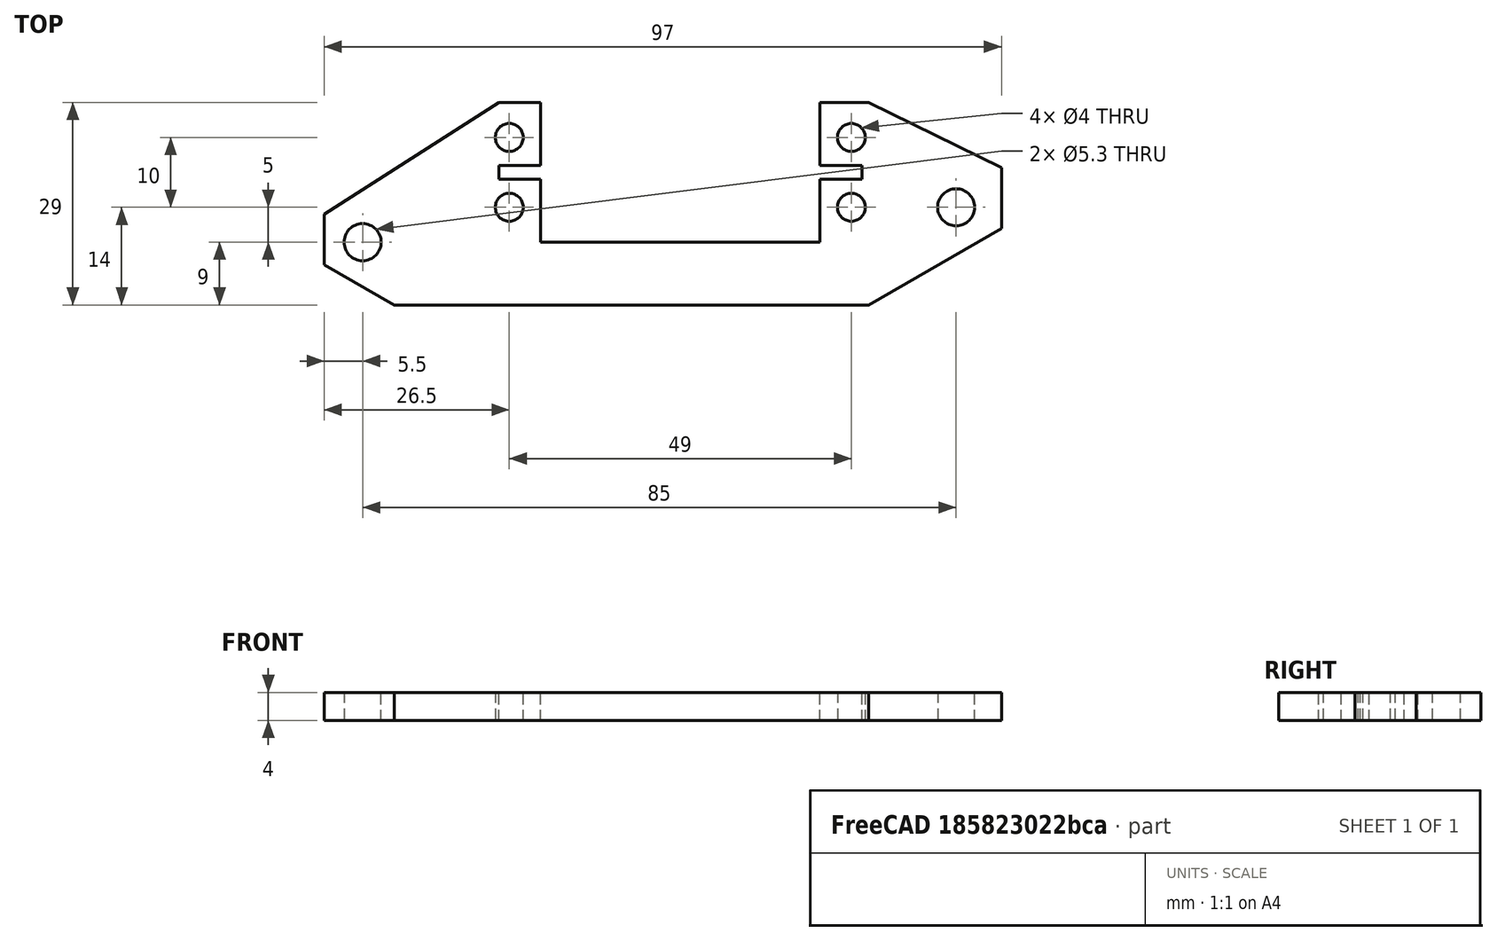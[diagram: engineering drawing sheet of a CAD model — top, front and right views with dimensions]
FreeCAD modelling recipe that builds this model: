
FCSTD DOCUMENT  (FreeCAD 0.19R24276 (Git))
Label: Servo_support_V4_long_oppozite_side_V1
License: All rights reserved
LicenseURL: http://en.wikipedia.org/wiki/All_rights_reserved
objects: Sketcher::SketchObject×1, PartDesign::Pad×1, PartDesign::Body×1
note: 4 computed .brp shape members not serialized (recipe doc carries the construction recipe); baked Part::Feature solids carry a one-line shape summary decoded from their .brp

FEATURE [Sketcher::SketchObject] Sketch005  label="Sketch005_54x20"
  AttachmentOffset = pos=(0,0,-5) rot=(0,0,1;0rad)
  FullyConstrained = false
  MapMode = 5
  Placement = pos=(0,0,-3) rot=(0,0,1;0rad)
  sketch-geometry (44):
    g0: GeomPoint X=1 Y=0 Z=0
    g1: GeomPoint X=1 Y=0 Z=0
    g2: GeomPoint X=1 Y=0 Z=0
    g3: GeomPoint X=1 Y=0 Z=0
    g4: Circle CenterX=-23.5 CenterY=5 CenterZ=0 NormalX=0 NormalY=0 NormalZ=1 AngleXU=0 Radius=2
    g5: Circle CenterX=-23.5 CenterY=-5 CenterZ=0 NormalX=0 NormalY=0 NormalZ=1 AngleXU=0 Radius=2
    g6: LineSegment StartX=1 StartY=0 StartZ=0 EndX=1 EndY=-5 EndZ=0
    g7: Circle CenterX=25.5 CenterY=5 CenterZ=0 NormalX=0 NormalY=0 NormalZ=1 AngleXU=0 Radius=2
    g8: Circle CenterX=25.5 CenterY=-5 CenterZ=0 NormalX=0 NormalY=0 NormalZ=1 AngleXU=0 Radius=2
    g9: LineSegment StartX=1 StartY=0 StartZ=0 EndX=-23.5 EndY=0 EndZ=0
    g10: LineSegment StartX=1 StartY=0 StartZ=0 EndX=49.8748 EndY=0 EndZ=0
    g11: ArcOfCircle CenterX=-7.75 CenterY=13.4234 CenterZ=0 NormalX=0 NormalY=0 NormalZ=1 AngleXU=0 Radius=9 StartAngle=0.290352 EndAngle=2.85124
    g12: LineSegment StartX=0 StartY=0 StartZ=0 EndX=-7.75 EndY=13.4234 EndZ=0
    g13: Circle CenterX=-44.5 CenterY=0 CenterZ=0 NormalX=0 NormalY=0 NormalZ=1 AngleXU=0 Radius=2.65
    g14: LineSegment StartX=-50 StartY=-19 StartZ=0 EndX=47 EndY=-19 EndZ=0
    g15: Circle CenterX=-44.5 CenterY=0 CenterZ=0 NormalX=0 NormalY=0 NormalZ=1 AngleXU=0 Radius=5.5
    g16: LineSegment StartX=-25 StartY=10 StartZ=0 EndX=-19 EndY=10 EndZ=0
    g17: LineSegment StartX=47 StartY=0.7 StartZ=0 EndX=47 EndY=-8.03034 EndZ=0
    g18: LineSegment StartX=-19 StartY=-10 StartZ=0 EndX=21 EndY=-10 EndZ=0
    g19: LineSegment StartX=21 StartY=-10 StartZ=0 EndX=21 EndY=-1 EndZ=0
    g20: Circle CenterX=40.5 CenterY=-5 CenterZ=0 NormalX=0 NormalY=0 NormalZ=1 AngleXU=0 Radius=2.65
    g21: Circle CenterX=40.5 CenterY=-5 CenterZ=0 NormalX=0 NormalY=0 NormalZ=1 AngleXU=0 Radius=5.5
    g22: LineSegment StartX=-19 StartY=-10 StartZ=0 EndX=-19 EndY=-1 EndZ=0
    g23: LineSegment StartX=-25 StartY=10 StartZ=0 EndX=-50 EndY=-6 EndZ=0
    g24: LineSegment StartX=-50 StartY=-6 StartZ=0 EndX=-50 EndY=-19 EndZ=0
    g25: LineSegment StartX=-50 StartY=-13.2265 StartZ=0 EndX=-40 EndY=-19 EndZ=0
    g26: LineSegment StartX=28 StartY=-19 StartZ=0 EndX=47 EndY=-8.03034 EndZ=0
    g27: LineSegment StartX=-50 StartY=-6 StartZ=0 EndX=-50 EndY=-13.2265 EndZ=0
    g28: LineSegment StartX=-40 StartY=-19 StartZ=0 EndX=28 EndY=-19 EndZ=0
    g29: LineSegment StartX=-25 StartY=1 StartZ=0 EndX=-19 EndY=1 EndZ=0
    g30: LineSegment StartX=-19 StartY=-1 StartZ=0 EndX=-25 EndY=-1 EndZ=0
    g31: LineSegment StartX=-25 StartY=-1 StartZ=0 EndX=-25 EndY=1 EndZ=0
    g32: LineSegment StartX=21 StartY=1 StartZ=0 EndX=27 EndY=1 EndZ=0
    g33: LineSegment StartX=27 StartY=1 StartZ=0 EndX=27 EndY=-1 EndZ=0
    g34: LineSegment StartX=27 StartY=-1 StartZ=0 EndX=21 EndY=-1 EndZ=0
    g35: LineSegment StartX=7.12713 StartY=-1 StartZ=0 EndX=7.12713 EndY=1 EndZ=0
    g36: LineSegment StartX=-23.5 StartY=0 StartZ=0 EndX=-25 EndY=0 EndZ=0
    g37: LineSegment StartX=-19 StartY=1 StartZ=0 EndX=-19 EndY=10 EndZ=0
    g38: LineSegment StartX=21 StartY=1 StartZ=0 EndX=21 EndY=10 EndZ=0
    g39: LineSegment StartX=21 StartY=10 StartZ=0 EndX=28 EndY=10 EndZ=0
    g40: LineSegment StartX=47 StartY=0.7 StartZ=0 EndX=28 EndY=10 EndZ=0
    g41: Circle CenterX=-44.5 CenterY=-10 CenterZ=0 NormalX=0 NormalY=0 NormalZ=1 AngleXU=0 Radius=2.65
    g42: Circle CenterX=-44.5 CenterY=-10 CenterZ=0 NormalX=0 NormalY=0 NormalZ=1 AngleXU=0 Radius=5.5
    g43: Circle CenterX=-10 CenterY=0 CenterZ=0 NormalX=0 NormalY=0 NormalZ=1 AngleXU=0 Radius=4.45958
  constraints (112):
    c: Coincident(g1,g0)
    c: Coincident(g3,g2)
    c: Coincident(g2,g0)
    c: Vertical(g5,g4)
    c: Coincident(g6,g0)
    c: Vertical(g6)
    c: Equal(g8,g7)
    c: Equal(g7,g5)
    c: Equal(g5,g4)
    c: Diameter(g8) = 4
    c: Vertical(g7,g8)
    c: Horizontal(g5,g8)
    c: Horizontal(g4,g7)
    c: Coincident(g9,g0)
    c: Horizontal(g9)
    c: Symmetric(g5,g4,g9)
    c: Coincident(g10,g0)
    c: Horizontal(g10)
    c: Symmetric(g5,g8,g6)
    c: DistanceY(g8,g7) = 10
    c: DistanceX(g5,g8) = 49
    c: Horizontal(g0,g-1)
    c: Diameter(g11) = 18
    c: Coincident(g12,g-1)
    c: Coincident(g12,g11)
    c: Angle(g10,g12) = 2.0944
    c: Distance(g11,g-1) = 15.5
    c: Diameter(g13) = 5.3
    c: Horizontal(g14)
    c: Coincident(g15,g13)
    c: Diameter(g15) = 11
    c: Horizontal(g16)
    c: DistanceY(g18,g0) = 10
    c: Horizontal(g18)
    c: Coincident(g19,g18)
    c: PointOnObject(g38,g16)
    c: Vertical(g19)
    c: DistanceX(g18,g18) = 40
    c: DistanceY(g14,g10) = 19
    c: Horizontal(g13,g0)
    c: DistanceX(g13,g-1) = 44.5
    c: Diameter(g20) = 5.3
    c: DistanceY(g20,g10) = 5
    c: DistanceX(g-1,g20) = 40.5
    c: DistanceX(g14,g-1) = 50
    c: DistanceX(g14,g14) = 97
    c: Vertical(g17)
    c: Coincident(g21,g20)
    c: Equal(g15,g21)
    c: DistanceY(g13,g16) = 10
    c: DistanceY(g23,g16) = 16
    c: Coincident(g22,g18)
    c: Coincident(g37,g16)
    c: Vertical(g22)
    c: Coincident(g23,g16)
    c: Coincident(g24,g23)
    c: Coincident(g24,g14)
    c: DistanceY(g14,g17) = 19.7
    c: Angle(g26,g14) = 2.61799
    c: Angle(g14,g25) = 2.61799
    c: PointOnObject(g26,g14)
    c: PointOnObject(g25,g14)
    c: DistanceX(g26,g17) = 19
    c: Coincident(g17,g26)
    c: DistanceX(g24,g25) = 10
    c: PointOnObject(g25,g24)
    c: Coincident(g27,g23)
    c: Coincident(g27,g25)
    c: Coincident(g28,g25)
    c: Coincident(g28,g26)
    c: DistanceX(g25,g17) = 97
    c: Coincident(g30,g31)
    c: Coincident(g31,g29)
    c: Horizontal(g29)
    c: Horizontal(g30)
    c: Vertical(g31)
    c: Coincident(g32,g33)
    c: Coincident(g33,g34)
    c: Horizontal(g32)
    c: Horizontal(g34)
    c: Vertical(g33)
    c: Vertical(g35)
    c: DistanceX(g29,g16) = 6
    c: Coincident(g36,g9)
    c: Horizontal(g36)
    c: Symmetric(g29,g30,g36)
    c: Coincident(g37,g29)
    c: Tangent(g22,g37)
    c: Coincident(g22,g30)
    c: DistanceY(g22,g37) = 2
    c: DistanceX(g38,g32) = 6
    c: Coincident(g38,g32)
    c: Tangent(g19,g38)
    c: Coincident(g19,g34)
    c: Horizontal(g29,g38)
    c: Horizontal(g19,g22)
    c: DistanceX(g16,g16) = 6
    c: Coincident(g39,g38)
    c: Horizontal(g39)
    c: Coincident(g40,g17)
    c: Coincident(g40,g39)
    c: DistanceX(g39,g39) = 7
    c: Coincident(g42,g41)
    c: Equal(g13,g41)
    c: Equal(g15,g42)
    c: Vertical(g13,g41)
    c: DistanceY(g41,g13) = 10
    c: Vertical(g27)
    c: PointOnObject(g43,g-1)
    c: DistanceX(g43,g-1) = 10
    c: DistanceX(g5,g18) = 4.5
    c: DistanceX(g5,g43) = 13.5
FEATURE [PartDesign::Pad] Pad
  Direction = (1,1,1)
  Length = 4
  Length2 = 100
  Placement = pos=(0,0,-3) rot=(0,0,1;0rad)
  Profile = -> Sketch005
  Type = 0
FEATURE [PartDesign::Body] Body
  Group = -> [Sketch005,Pad]
  Origin = -> Origin
  Tip = -> Pad
